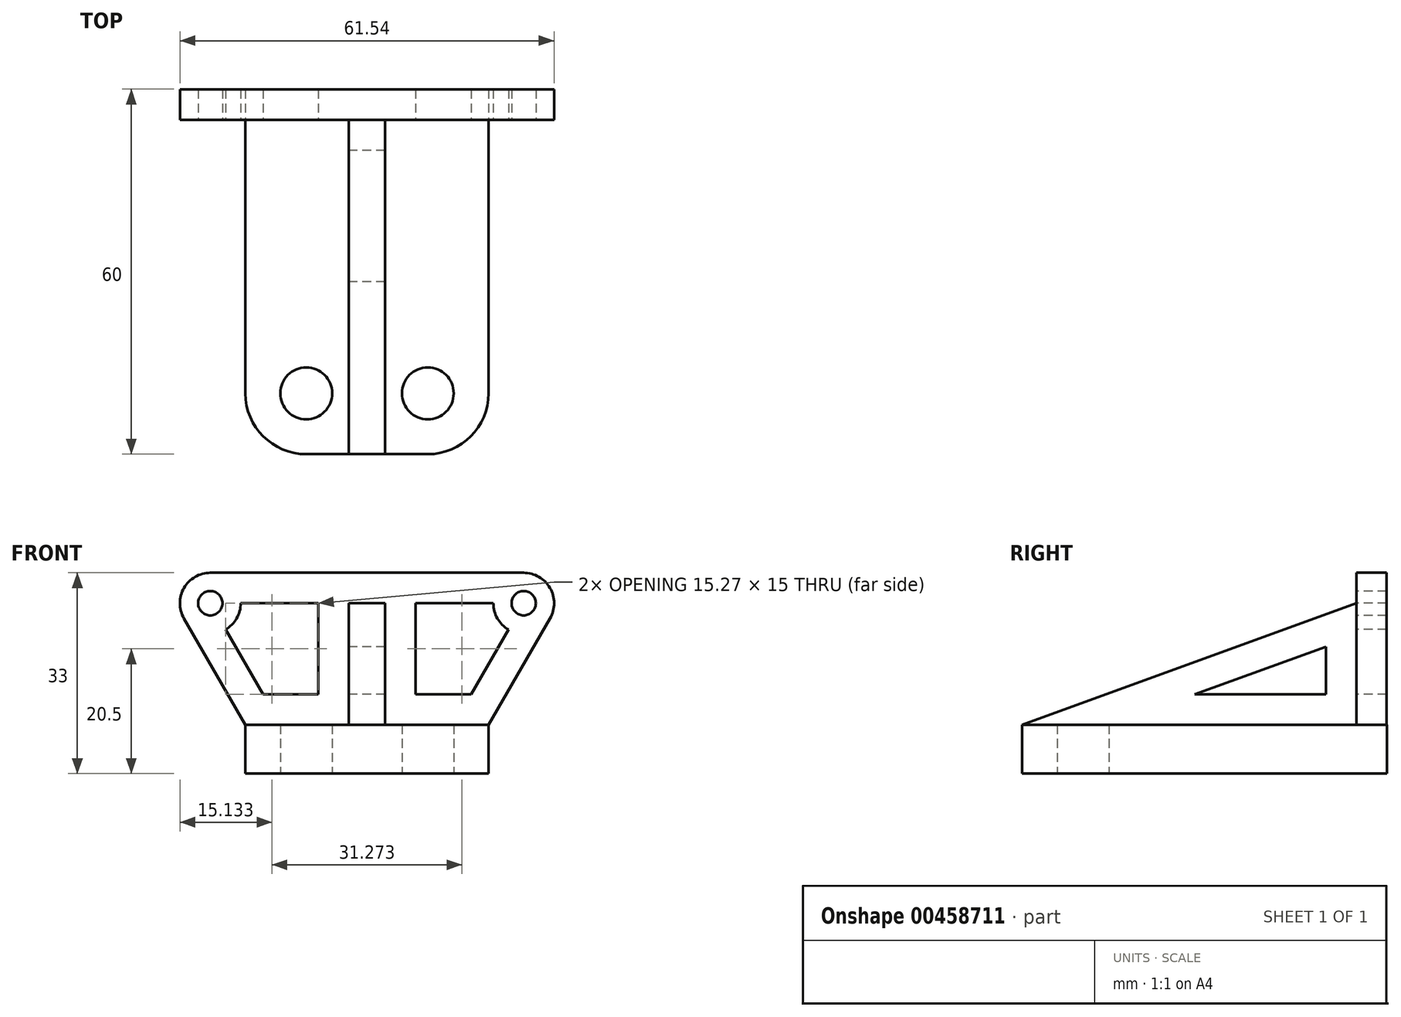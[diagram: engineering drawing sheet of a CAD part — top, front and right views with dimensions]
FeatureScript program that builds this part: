
annotation { "Feature Type Name" : "Feature", "Feature Type Description" : "" }
export const myFeature = defineFeature(function(context is Context, id is Id, definition is map)
    precondition{}
    {
        {
            var Q0;
            Q0=qCreatedBy(makeId("Top.planeOp"),FACE);
            var sketch = newSketch(context, id + "F0", { "sketchPlane" : qUnion([Q0])});
            skLineSegment(sketch, "E0", {"start": v(-20, 26.29) * mm, "end": v(-20, -23.71) * mm});
            skLineSegment(sketch, "E1", {"start": v(-10, -33.71) * mm, "end": v(10, -33.71) * mm});
            skLineSegment(sketch, "E2", {"start": v(20, 26.29) * mm, "end": v(20, -23.71) * mm});
            skLineSegment(sketch, "E3", {"start": v(-20, 26.29) * mm, "end": v(20, 26.29) * mm});
            skPoint(sketch, "E4.visualSharp", {"position": v(-20, -33.71) * mm});
            skArc(sketch, "E4.filletArc", {"start": v(-20, -23.71) * mm, "mid": v(-17.07, -30.78) * mm, "end": v(-10, -33.71) * mm});
            skPoint(sketch, "E5.visualSharp", {"position": v(20, -33.71) * mm});
            skArc(sketch, "E5.filletArc", {"start": v(10, -33.71) * mm, "mid": v(17.07, -30.78) * mm, "end": v(20, -23.71) * mm});
            skCircle(sketch, "E6", {"center": v(-10, -23.71) * mm, "radius": 4.27 * mm});
            skLineSegment(sketch, "E7", {"start": v(0, 26.29) * mm, "end": v(0, -33.71) * mm, "construction": true});
            skCircle(sketch, "E8.MirrorC", {"center": v(10, -23.71) * mm, "radius": 4.27 * mm});
            skSolve(sketch);
        }
        {
            var Q0;
            Q0 = qSketchRegion(id + "F0", true);
            extrude(context, id + "F1", {"entities" : qUnion([Q0]), "depth" : 8 * mm});
        }
        {
            var Q0;
            Q0=qCreatedBy(makeId("Right.planeOp"),FACE);
            var sketch = newSketch(context, id + "F2", { "sketchPlane" : qUnion([Q0])});
            skLineSegment(sketch, "E9", {"start": v(-33.71, 8) * mm, "end": v(21.24, 28) * mm});
            skLineSegment(sketch, "E10", {"start": v(21.24, 28) * mm, "end": v(21.24, 8) * mm});
            skLineSegment(sketch, "E11", {"start": v(21.24, 8) * mm, "end": v(-33.71, 8) * mm});
            skLineSegment(sketch, "E12.0", {"start": v(-5.36, 13) * mm, "end": v(16.24, 20.86) * mm});
            skLineSegment(sketch, "E12.1", {"start": v(16.24, 13) * mm, "end": v(-5.36, 13) * mm});
            skLineSegment(sketch, "E12.2", {"start": v(16.24, 20.86) * mm, "end": v(16.24, 13) * mm});
            skSolve(sketch);
        }
        {
            var Q0;
            Q0=makeQuery(id+"F2.imprint","IMPRINT",FACE,{"disambiguationData":[TD([[makeQuery(id+"F2.imprint","IMPRINT",EDGE,{"derivedFrom":sQuery(id+"F2.wireOp",EDGE,"E9")}),-1.0]])]});
            extrude(context, id + "F3", {"entities" : qUnion([Q0]), "operationType" : NewBodyOperationType.ADD, "depth" : 6 * mm, "symmetric" : true});
        }
        {
            var Q0;
            Q0=makeQuery(id+"F3.opExtrude","SWEPT_FACE",FACE,{"disambiguationData":[OSD([sQuery(id+"F2.wireOp",EDGE,"E10")])]});
            var sketch = newSketch(context, id + "F4", { "sketchPlane" : qUnion([Q0])});
            skLineSegment(sketch, "E13", {"start": v(-20, 8) * mm, "end": v(20, 8) * mm});
            skLineSegment(sketch, "E14", {"start": v(-20, 8) * mm, "end": v(-30.1, 25.5) * mm});
            skLineSegment(sketch, "E15", {"start": v(0, 28) * mm, "end": v(0, 8) * mm, "construction": true});
            skCircle(sketch, "E16", {"center": v(-25.77, 28) * mm, "radius": 5 * mm});
            skCircle(sketch, "E17", {"center": v(-25.77, 28) * mm, "radius": 2 * mm});
            skLineSegment(sketch, "E18", {"start": v(-25.77, 33) * mm, "end": v(0, 33) * mm});
            skLineSegment(sketch, "E19", {"start": v(-23.27, 23.67) * mm, "end": v(-17.11, 13) * mm});
            skLineSegment(sketch, "E20", {"start": v(-17.11, 13) * mm, "end": v(-8, 13) * mm});
            skLineSegment(sketch, "E21", {"start": v(-8, 13) * mm, "end": v(-8, 28) * mm});
            skLineSegment(sketch, "E22", {"start": v(-8, 28) * mm, "end": v(-20.77, 28) * mm});
            skLineSegment(sketch, "E23.MirrorCS", {"start": v(25.77, 33) * mm, "end": v(0, 33) * mm});
            skLineSegment(sketch, "E24.MirrorCS", {"start": v(8, 28) * mm, "end": v(20.77, 28) * mm});
            skLineSegment(sketch, "E25.MirrorCS", {"start": v(8, 13) * mm, "end": v(8, 28) * mm});
            skLineSegment(sketch, "E26.MirrorCS", {"start": v(17.11, 13) * mm, "end": v(8, 13) * mm});
            skLineSegment(sketch, "E27.MirrorCS", {"start": v(23.27, 23.67) * mm, "end": v(17.11, 13) * mm});
            skCircle(sketch, "E28.MirrorC", {"center": v(25.77, 28) * mm, "radius": 5 * mm});
            skCircle(sketch, "E29.MirrorC", {"center": v(25.77, 28) * mm, "radius": 2 * mm});
            skLineSegment(sketch, "E30.MirrorCS", {"start": v(20, 8) * mm, "end": v(30.1, 25.5) * mm});
            skSolve(sketch);
        }
        {
            var Q0;
            Q0 = qSketchRegion(id + "F4", true);
            extrude(context, id + "F5", {"entities" : qUnion([Q0]), "operationType" : NewBodyOperationType.ADD, "depth" : 5 * mm});
        }
    });
